# Revit family: Saxi Kastbur
name_source: partatom
category: Generic Models
revit_build: Autodesk Revit 2017 (Build: 20160225_1515(x64)
units: mm (PartAtom-declared; Revit-internal decimal feet)

## family parameters
Always vertical = Yes
Can host rebar = No
Cut with Voids When Loaded = No
Part Type = Normal
Room Calculation Point = No
Round Connector Dimension = Use Diameter
Shared = No
Work Plane-Based = No

## types (1)
- Saxi Kastbur
    Height = 8000 mm  [stored 26.2467 ft]
    Height brackets = 8040 mm  [stored 26.378 ft]
    Height brackets 2 = 8044 mm  [stored 26.3911 ft]
    Height lift frame = 200 mm  [stored 0.656168 ft]
    Height tissue = 7900 mm  [stored 25.9186 ft]
    Height wirsbotissue = 7450 mm  [stored 24.4423 ft]
    Manufacturer = Saxi Vägg AB
    Model = Saxi Throwing Cage
    Shaft = 8201 mm  [stored 26.9062 ft]
    URL = http://www.saxi.se

note: [stored X ft] marks values corroborated as IEEE doubles in the binary element streams (Revit-internal decimal feet)

## geometry (parser evidence)
native form markers: Blend x6, Sweep x40
no freeform markers — native parametric forms only
